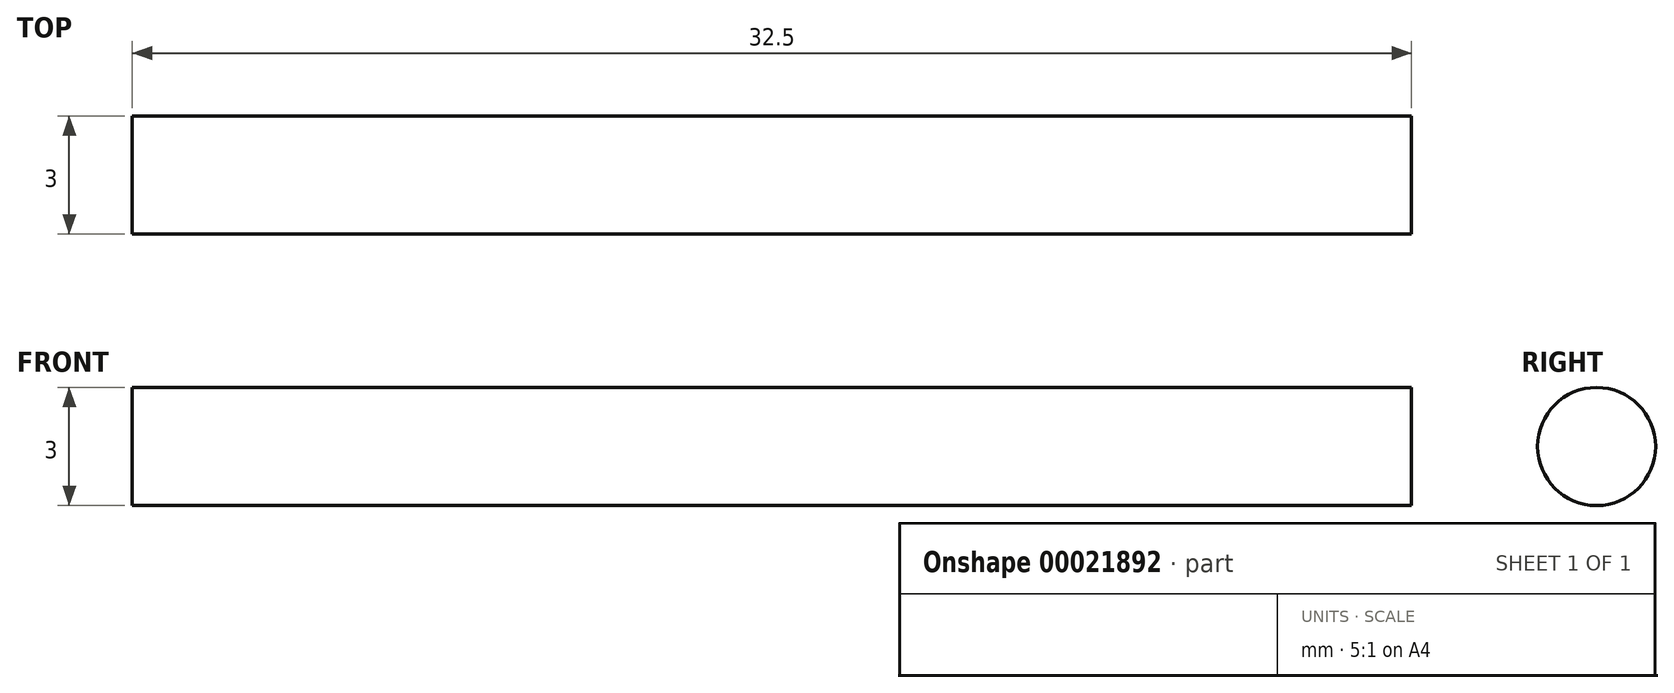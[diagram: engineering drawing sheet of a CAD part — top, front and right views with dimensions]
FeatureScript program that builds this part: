
annotation { "Feature Type Name" : "Feature", "Feature Type Description" : "" }
export const myFeature = defineFeature(function(context is Context, id is Id, definition is map)
    precondition{}
    {
        {
            var Q0;
            Q0=qCreatedBy(makeId("Front.planeOp"),FACE);
            var sketch = newSketch(context, id + "F0", { "sketchPlane" : qUnion([Q0])});
            skLineSegment(sketch, "E0", {"start": v(-16.25, 0) * mm, "end": v(16.25, 0) * mm});
            skLineSegment(sketch, "E1", {"start": v(-16.25, 1.5) * mm, "end": v(16.25, 1.5) * mm});
            skLineSegment(sketch, "E2", {"start": v(0, 0) * mm, "end": v(0, 1.5) * mm});
            skLineSegment(sketch, "E3", {"start": v(-16.25, 1.5) * mm, "end": v(-16.25, 0) * mm});
            skLineSegment(sketch, "E4", {"start": v(16.25, 1.5) * mm, "end": v(16.25, 0) * mm});
            skSolve(sketch);
        }
        {
            var Q0;
            {var subQ1=sQuery(id+"F0.wireOp",EDGE,"E2");Q0=makeQuery(id+"F0.imprint","IMPRINT",FACE,{"disambiguationData":[TD([[makeQuery(id+"F0.imprint","IMPRINT",EDGE,{"derivedFrom":subQ1}),1.0]])]});}
            var Q1;
            {var subQ1=sQuery(id+"F0.wireOp",EDGE,"E2");Q1=makeQuery(id+"F0.imprint","IMPRINT",FACE,{"disambiguationData":[TD([[makeQuery(id+"F0.imprint","IMPRINT",EDGE,{"derivedFrom":subQ1}),-1.0]])]});}
            var Q2;
            Q2=sQuery(id+"F0.wireOp",EDGE,"E0");
            revolve(context, id + "F1", {"entities" : qUnion([Q0, Q1]), "axis" : qUnion([Q2]), "revolveType" : RevolveType.FULL});
        }
    });
